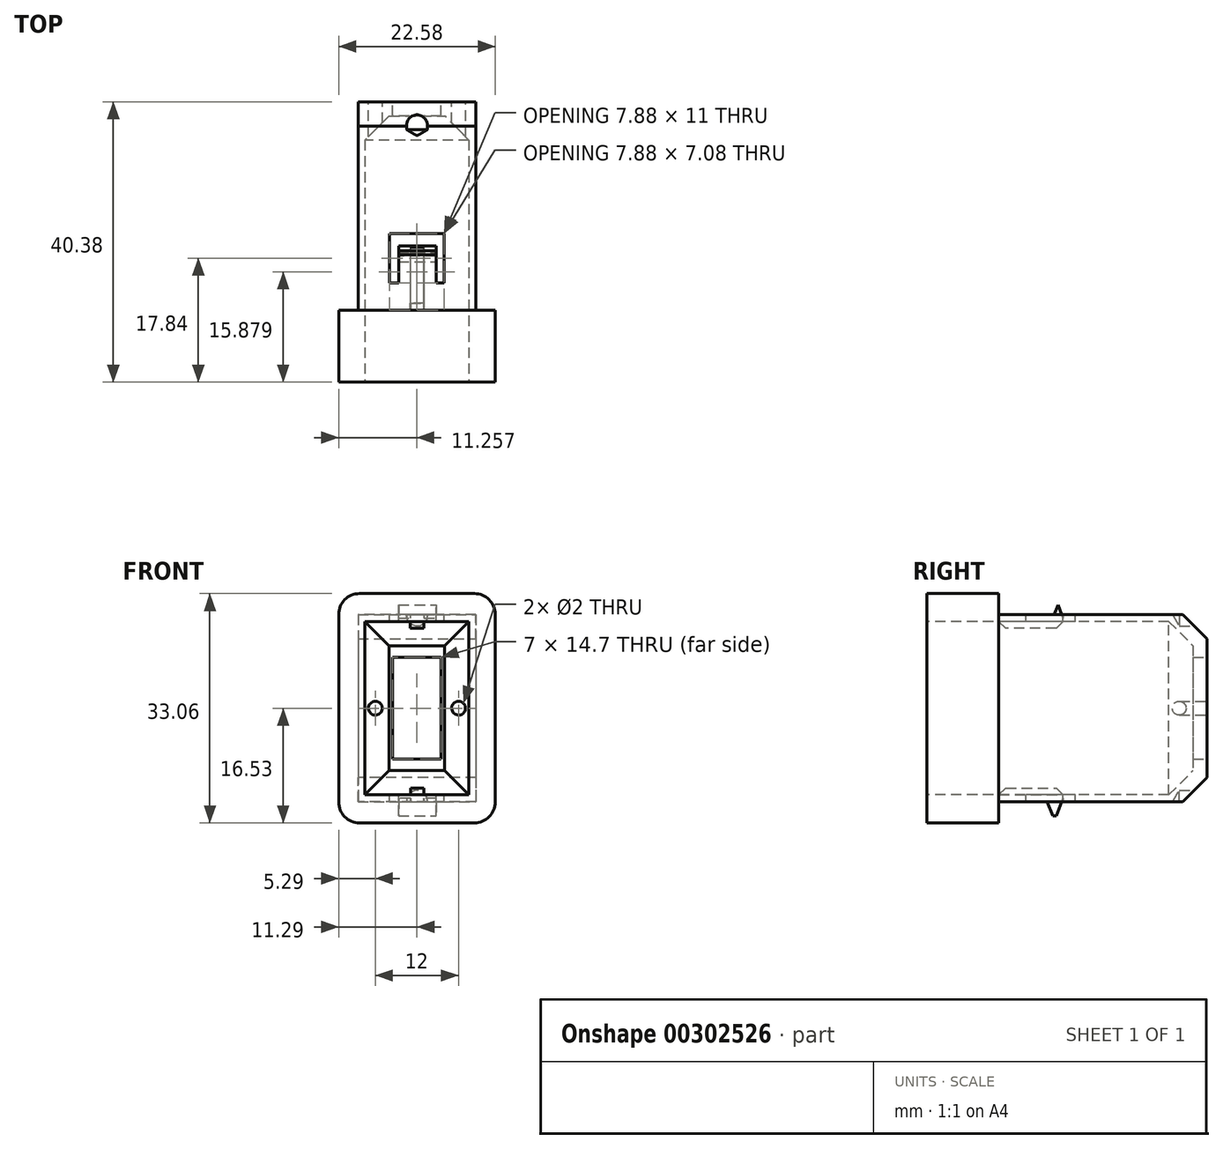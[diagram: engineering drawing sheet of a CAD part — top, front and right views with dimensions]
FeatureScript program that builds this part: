
annotation { "Feature Type Name" : "Feature", "Feature Type Description" : "" }
export const myFeature = defineFeature(function(context is Context, id is Id, definition is map)
    precondition{}
    {
        {
            assignVariable(context, id + "F0", {"name" : "face_depth", "anyValue" : 10.38});
        }
        {
            assignVariable(context, id + "F1", {"name" : "neck_height", "anyValue" : 27});
        }
        {
            assignVariable(context, id + "F2", {"name" : "neck_tab_hieght", "anyValue" : 31});
        }
        {
            assignVariable(context, id + "F3", {"name" : "neck_depth", "anyValue" : 30});
        }
        {
            var Q0;
            Q0=qCreatedBy(makeId("Front.planeOp"),FACE);
            var sketch = newSketch(context, id + "F4", { "sketchPlane" : qUnion([Q0])});
            skLineSegment(sketch, "E0.bottom", {"start": v(8.5, 13.5) * mm, "end": v(-8.5, 13.5) * mm});
            skLineSegment(sketch, "E0.top", {"start": v(8.5, -13.5) * mm, "end": v(-8.5, -13.5) * mm});
            skLineSegment(sketch, "E0.left", {"start": v(8.5, 13.5) * mm, "end": v(8.5, -13.5) * mm});
            skLineSegment(sketch, "E0.right", {"start": v(-8.5, 13.5) * mm, "end": v(-8.5, -13.5) * mm});
            skPoint(sketch, "E0.middle", {"position": v(0, 0) * mm});
            skLineSegment(sketch, "E1.bottom", {"start": v(11.29, -16.52) * mm, "end": v(-11.29, -16.53) * mm});
            skLineSegment(sketch, "E1.top", {"start": v(11.3, 16.52) * mm, "end": v(-11.29, 16.52) * mm});
            skLineSegment(sketch, "E1.left", {"start": v(11.29, -16.52) * mm, "end": v(11.3, 16.52) * mm});
            skLineSegment(sketch, "E1.right", {"start": v(-11.29, -16.52) * mm, "end": v(-11.29, 16.52) * mm});
            skSolve(sketch);
        }
        {
            var Q0;
            Q0=makeQuery(id+"F4.imprint","IMPRINT",FACE,{"disambiguationData":[TD([[makeQuery(id+"F4.imprint","IMPRINT",EDGE,{"derivedFrom":sQuery(id+"F4.wireOp",EDGE,"E0.bottom")}),1.0]])]});
            extrude(context, id + "F5", {"entities" : qUnion([Q0]), "oppositeDirection" : true, "depth" : (getVariable(context, 'neck_depth')) * mm});
        }
        {
            var Q0;
            Q0=makeQuery(id+"F4.imprint","IMPRINT",FACE,{"disambiguationData":[TD([[makeQuery(id+"F4.imprint","IMPRINT",EDGE,{"derivedFrom":sQuery(id+"F4.wireOp",EDGE,"E0.bottom")}),-1.0]])]});
            var Q1;
            Q1=makeQuery(id+"F4.imprint","IMPRINT",FACE,{"disambiguationData":[TD([[makeQuery(id+"F4.imprint","IMPRINT",EDGE,{"derivedFrom":sQuery(id+"F4.wireOp",EDGE,"E0.bottom")}),1.0]])]});
            extrude(context, id + "F6", {"entities" : qUnion([Q0, Q1]), "operationType" : NewBodyOperationType.ADD, "depth" : (getVariable(context, 'face_depth')) * mm});
        }
        {
            var Q0;
            Q0=makeQuery(id+"F6.opExtrude","CAP_FACE",FACE,{"disambiguationData":[OSD([sQuery(id+"F4.wireOp",EDGE,"E1.bottom"),sQuery(id+"F4.wireOp",EDGE,"E1.top"),sQuery(id+"F4.wireOp",EDGE,"E1.left"),sQuery(id+"F4.wireOp",EDGE,"E1.right")])],"isStart":false});
            var sketch = newSketch(context, id + "F7", { "sketchPlane" : qUnion([Q0])});
            skLineSegment(sketch, "E2.bottom", {"start": v(-7.5, 12.5) * mm, "end": v(7.5, 12.5) * mm});
            skLineSegment(sketch, "E2.top", {"start": v(-7.5, -12.5) * mm, "end": v(7.5, -12.5) * mm});
            skLineSegment(sketch, "E2.left", {"start": v(-7.5, 12.5) * mm, "end": v(-7.5, -12.5) * mm});
            skLineSegment(sketch, "E2.right", {"start": v(7.5, 12.5) * mm, "end": v(7.5, -12.5) * mm});
            skPoint(sketch, "E2.middle", {"position": v(0, 0) * mm});
            skSolve(sketch);
        }
        {
            var Q0;
            Q0=makeQuery(id+"F7.imprint","IMPRINT",FACE,{"disambiguationData":[TD([[makeQuery(id+"F7.imprint","IMPRINT",EDGE,{"derivedFrom":sQuery(id+"F7.wireOp",EDGE,"E2.bottom")}),-1.0]])]});
            extrude(context, id + "F8", {"entities" : qUnion([Q0]), "operationType" : NewBodyOperationType.REMOVE, "oppositeDirection" : true, "depth" : (getVariable(context, 'face_depth') + getVariable(context, 'neck_depth') - 2) * mm});
        }
        {
            var Q0;
            Q0=makeQuery(id+"F5.opExtrude","CAP_FACE",FACE,{"disambiguationData":[OSD([sQuery(id+"F4.wireOp",EDGE,"E0.bottom"),sQuery(id+"F4.wireOp",EDGE,"E0.top"),sQuery(id+"F4.wireOp",EDGE,"E0.left"),sQuery(id+"F4.wireOp",EDGE,"E0.right")])],"isStart":false});
            var sketch = newSketch(context, id + "F9", { "sketchPlane" : qUnion([Q0])});
            skLineSegment(sketch, "E3.bottom", {"start": v(3.5, -7.35) * mm, "end": v(-3.5, -7.35) * mm});
            skLineSegment(sketch, "E3.top", {"start": v(3.5, 7.35) * mm, "end": v(-3.5, 7.35) * mm});
            skLineSegment(sketch, "E3.left", {"start": v(3.5, -7.35) * mm, "end": v(3.5, 7.35) * mm});
            skLineSegment(sketch, "E3.right", {"start": v(-3.5, -7.35) * mm, "end": v(-3.5, 7.35) * mm});
            skPoint(sketch, "E3.middle", {"position": v(0, 0) * mm});
            skSolve(sketch);
        }
        {
            var Q0;
            Q0=makeQuery(id+"F9.imprint","IMPRINT",FACE,{"disambiguationData":[TD([[makeQuery(id+"F9.imprint","IMPRINT",EDGE,{"derivedFrom":sQuery(id+"F9.wireOp",EDGE,"E3.bottom")}),-1.0]])]});
            extrude(context, id + "F10", {"entities" : qUnion([Q0]), "operationType" : NewBodyOperationType.REMOVE, "oppositeDirection" : true, "depth" : 25 * mm});
        }
        {
            var Q0;
            Q0=makeQuery(id+"F5.opExtrude","SWEPT_FACE",FACE,{"disambiguationData":[OSD([sQuery(id+"F4.wireOp",EDGE,"E0.bottom")])]});
            var sketch = newSketch(context, id + "F11", { "sketchPlane" : qUnion([Q0])});
            skLineSegment(sketch, "E4.bottom", {"start": v(-3.97, 3.92) * mm, "end": v(3.9, 3.92) * mm});
            skLineSegment(sketch, "E4.top", {"start": v(-3.97, 11) * mm, "end": v(3.9, 11) * mm});
            skLineSegment(sketch, "E4.left", {"start": v(-3.97, 3.92) * mm, "end": v(-3.97, 11) * mm});
            skLineSegment(sketch, "E4.right", {"start": v(3.9, 3.92) * mm, "end": v(3.9, 11) * mm});
            skLineSegment(sketch, "E5.bottom", {"start": v(-2.64, 3.92) * mm, "end": v(2.75, 3.92) * mm});
            skLineSegment(sketch, "E5.top", {"start": v(-2.64, 9.27) * mm, "end": v(2.75, 9.27) * mm});
            skLineSegment(sketch, "E5.left", {"start": v(-2.64, 3.92) * mm, "end": v(-2.64, 9.27) * mm});
            skLineSegment(sketch, "E5.right", {"start": v(2.75, 3.92) * mm, "end": v(2.75, 9.27) * mm});
            skLineSegment(sketch, "E6", {"start": v(-2.64, 7.77) * mm, "end": v(2.75, 7.77) * mm});
            skSolve(sketch);
        }
        {
            var Q0;
            Q0=makeQuery(id+"F11.imprint","IMPRINT",FACE,{"disambiguationData":[TD([[makeQuery(id+"F11.imprint","IMPRINT",EDGE,{"derivedFrom":sQuery(id+"F11.wireOp",EDGE,"E4.top")}),-1.0]])]});
            extrude(context, id + "F12", {"entities" : qUnion([Q0]), "operationType" : NewBodyOperationType.REMOVE, "oppositeDirection" : true, "depth" : 100 * mm});
        }
        {
            var Q0;
            {var subQ0=sQuery(id+"F11.wireOp",EDGE,"E5.top");Q0=makeQuery(id+"F11.imprint","IMPRINT",FACE,{"disambiguationData":[TD([[makeQuery(id+"F11.imprint","IMPRINT",EDGE,{"derivedFrom":subQ0}),-1.0]])]});}
            extrude(context, id + "F13", {"entities" : qUnion([Q0]), "operationType" : NewBodyOperationType.ADD, "depth" : (getVariable(context, 'neck_tab_hieght') - getVariable(context, 'neck_height')) / 2 * mm});
        }
        {
            var Q0;
            Q0=makeQuery(id+"F13.opExtrude","CAP_EDGE",EDGE,{"disambiguationData":[OSD([sQuery(id+"F11.wireOp",EDGE,"E6")])],"isStart":false});
            var Q1;
            Q1=makeQuery(id+"F13.opExtrude","CAP_EDGE",EDGE,{"disambiguationData":[OSD([sQuery(id+"F11.wireOp",EDGE,"E5.top")])],"isStart":false});
            chamfer(context, id + "F14", {"entities" : qUnion([Q0, Q1]), "chamferType" : ChamferType.TWO_OFFSETS, "width1" : 1 * mm, "oppositeDirection" : false, "width2" : 2.5 * mm, "tangentPropagation" : true});
        }
        {
            var Q0;
            Q0=makeQuery(id+"F5.opExtrude","SWEPT_FACE",FACE,{"disambiguationData":[OSD([sQuery(id+"F4.wireOp",EDGE,"E0.top")])]});
            var sketch = newSketch(context, id + "F15", { "sketchPlane" : qUnion([Q0])});
            skLineSegment(sketch, "E7", {"start": v(2.75, -6.77) * mm, "end": v(-2.64, -6.77) * mm});
            skSolve(sketch);
        }
        {
            var Q0;
            {var subQ0=sQuery(id+"F15.wireOp",EDGE,"E7");Q0=makeQuery(id+"F15.imprint","IMPRINT",FACE,{"disambiguationData":[TD([[makeQuery(id+"F15.imprint","IMPRINT",EDGE,{"derivedFrom":subQ0}),1.0]])]});}
            extrude(context, id + "F16", {"entities" : qUnion([Q0]), "operationType" : NewBodyOperationType.ADD, "depth" : (getVariable(context, 'neck_tab_hieght') - getVariable(context, 'neck_height')) / 2 * mm});
        }
        {
            var Q0;
            Q0=makeQuery(id+"F16.opExtrude","CAP_EDGE",EDGE,{"disambiguationData":[OSD([sQuery(id+"F15.wireOp",EDGE,"E7")])],"isStart":false});
            var Q1;
            Q1=makeQuery(id+"F16.opExtrude","CAP_EDGE",EDGE,{"disambiguationData":[OSD([sQuery(id+"F4.wireOp",EDGE,"E0.top"),sQuery(id+"F11.wireOp",EDGE,"E5.top")])],"isStart":false});
            chamfer(context, id + "F17", {"entities" : qUnion([Q0, Q1]), "chamferType" : ChamferType.TWO_OFFSETS, "width1" : 1 * mm, "oppositeDirection" : false, "width2" : 2.5 * mm, "tangentPropagation" : true});
        }
        {
            var Q0;
            Q0=makeQuery(id+"F8.boolean.opBoolean","COPY",EDGE,{"derivedFrom":makeQuery(id+"F8.opExtrude","CAP_EDGE",EDGE,{"disambiguationData":[OSD([sQuery(id+"F7.wireOp",EDGE,"E2.right")])],"isStart":false})});
            var Q1;
            Q1=makeQuery(id+"F8.boolean.opBoolean","COPY",EDGE,{"derivedFrom":makeQuery(id+"F8.opExtrude","CAP_EDGE",EDGE,{"disambiguationData":[OSD([sQuery(id+"F7.wireOp",EDGE,"E2.left")])],"isStart":false})});
            var Q2;
            Q2=makeQuery(id+"F8.boolean.opBoolean","COPY",EDGE,{"derivedFrom":makeQuery(id+"F8.opExtrude","CAP_EDGE",EDGE,{"disambiguationData":[OSD([sQuery(id+"F7.wireOp",EDGE,"E2.bottom")])],"isStart":false})});
            var Q3;
            Q3=makeQuery(id+"F8.boolean.opBoolean","COPY",EDGE,{"derivedFrom":makeQuery(id+"F8.opExtrude","CAP_EDGE",EDGE,{"disambiguationData":[OSD([sQuery(id+"F7.wireOp",EDGE,"E2.top")])],"isStart":false})});
            var Q4;
            Q4=makeQuery(id+"F5.opExtrude","CAP_EDGE",EDGE,{"disambiguationData":[OSD([sQuery(id+"F4.wireOp",EDGE,"E0.bottom")])],"isStart":false});
            var Q5;
            Q5=makeQuery(id+"F5.opExtrude","CAP_EDGE",EDGE,{"disambiguationData":[OSD([sQuery(id+"F4.wireOp",EDGE,"E0.top")])],"isStart":false});
            chamfer(context, id + "F18", {"entities" : qUnion([Q0, Q1, Q2, Q3, Q4, Q5]), "width" : 3.5 * mm, "tangentPropagation" : true});
        }
        {
            var Q0;
            Q0=makeQuery(id+"F6.opExtrude","SWEPT_EDGE",EDGE,{"disambiguationData":[OSD([sQuery(id+"F4.wireOp",EDGE,"E1.top"),sQuery(id+"F4.wireOp",EDGE,"E1.right")])]});
            var Q1;
            Q1=makeQuery(id+"F6.opExtrude","SWEPT_EDGE",EDGE,{"disambiguationData":[OSD([sQuery(id+"F4.wireOp",EDGE,"E1.top"),sQuery(id+"F4.wireOp",EDGE,"E1.left")])]});
            var Q2;
            Q2=makeQuery(id+"F6.opExtrude","SWEPT_EDGE",EDGE,{"disambiguationData":[OSD([sQuery(id+"F4.wireOp",EDGE,"E1.bottom"),sQuery(id+"F4.wireOp",EDGE,"E1.left")])]});
            var Q3;
            Q3=makeQuery(id+"F6.opExtrude","SWEPT_EDGE",EDGE,{"disambiguationData":[OSD([sQuery(id+"F4.wireOp",EDGE,"E1.bottom"),sQuery(id+"F4.wireOp",EDGE,"E1.right")])]});
            fillet(context, id + "F19", {"entities" : qUnion([Q0, Q1, Q2, Q3]), "radius" : 3 * mm, "tangentPropagation" : true, "allowEdgeOverflow" : false});
        }
        {
            var Q0;
            Q0=makeQuery(id+"F5.opExtrude","CAP_FACE",FACE,{"disambiguationData":[OSD([sQuery(id+"F4.wireOp",EDGE,"E0.bottom"),sQuery(id+"F4.wireOp",EDGE,"E0.top"),sQuery(id+"F4.wireOp",EDGE,"E0.left"),sQuery(id+"F4.wireOp",EDGE,"E0.right")])],"isStart":false});
            var sketch = newSketch(context, id + "F20", { "sketchPlane" : qUnion([Q0])});
            skPoint(sketch, "E8", {"position": v(-6, 0) * mm});
            skPoint(sketch, "E8.positionSnap0", {"position": v(-3.5, 0) * mm});
            skPoint(sketch, "E9", {"position": v(6, 0) * mm});
            skPoint(sketch, "E9.positionSnap0", {"position": v(3.5, 0) * mm});
            skPoint(sketch, "E10", {"position": v(0, 13.35) * mm});
            skPoint(sketch, "E10.positionSnap0", {"position": v(0, 7.35) * mm});
            skPoint(sketch, "E11", {"position": v(0, -13.35) * mm});
            skPoint(sketch, "E11.positionSnap0", {"position": v(0, -7.35) * mm});
            skSolve(sketch);
        }
        {
            var Q0;
            Q0=sQuery(id+"F20.wireOp",VERTEX,"E8");
            var Q1;
            Q1=sQuery(id+"F20.wireOp",VERTEX,"E9");
            var Q2;
            Q2=makeQuery(id+"F5.opExtrude","SWEPT_BODY",BODY,{"disambiguationData":[OSD([sQuery(id+"F4.wireOp",EDGE,"E0.bottom"),sQuery(id+"F4.wireOp",EDGE,"E0.top"),sQuery(id+"F4.wireOp",EDGE,"E0.left"),sQuery(id+"F4.wireOp",EDGE,"E0.right")])]});
            hole(context, id + "F21", {"style" : HoleStyle.SIMPLE, "endStyle" : HoleEndStyle.BLIND, "holeDiameter" : 2 * mm, "holeDepth" : 6 * mm, "isTappedThrough" : true, "tappedDepth" : 12 * mm, "tapClearance" : 3, "locations" : qUnion([Q0, Q1]), "scope" : qUnion([Q2])});
        }
        {
            var Q0;
            Q0=sQuery(id+"F20.wireOp",VERTEX,"E10");
            var Q1;
            Q1=sQuery(id+"F20.wireOp",VERTEX,"E11");
            var Q2;
            Q2=makeQuery(id+"F5.opExtrude","SWEPT_BODY",BODY,{"disambiguationData":[OSD([sQuery(id+"F4.wireOp",EDGE,"E0.bottom"),sQuery(id+"F4.wireOp",EDGE,"E0.top"),sQuery(id+"F4.wireOp",EDGE,"E0.left"),sQuery(id+"F4.wireOp",EDGE,"E0.right")])]});
            hole(context, id + "F22", {"style" : HoleStyle.SIMPLE, "endStyle" : HoleEndStyle.BLIND, "holeDiameter" : 3 * mm, "holeDepth" : 4 * mm, "isTappedThrough" : true, "tappedDepth" : 12 * mm, "tapClearance" : 3, "locations" : qUnion([Q0, Q1]), "scope" : qUnion([Q2])});
        }
        {
            var Q0;
            Q0=makeQuery(id+"F8.boolean.opBoolean","COPY",FACE,{"derivedFrom":makeQuery(id+"F8.opExtrude","SWEPT_FACE",FACE,{"disambiguationData":[OSD([sQuery(id+"F7.wireOp",EDGE,"E2.bottom")])]})});
            var sketch = newSketch(context, id + "F23", { "sketchPlane" : qUnion([Q0])});
            skLineSegment(sketch, "E12.bottom", {"start": v(1, -9.27) * mm, "end": v(-0.95, -9.27) * mm});
            skLineSegment(sketch, "E12.top", {"start": v(1, 0) * mm, "end": v(-0.95, 0) * mm});
            skLineSegment(sketch, "E12.left", {"start": v(1, -9.27) * mm, "end": v(1, 0) * mm});
            skLineSegment(sketch, "E12.right", {"start": v(-0.95, -9.27) * mm, "end": v(-0.95, 0) * mm});
            skPoint(sketch, "E12.middle", {"position": v(0.03, -4.63) * mm});
            skSolve(sketch);
        }
        {
            var Q0;
            Q0=makeQuery(id+"F8.boolean.opBoolean","COPY",FACE,{"derivedFrom":makeQuery(id+"F8.opExtrude","SWEPT_FACE",FACE,{"disambiguationData":[OSD([sQuery(id+"F7.wireOp",EDGE,"E2.top")])]})});
            var sketch = newSketch(context, id + "F24", { "sketchPlane" : qUnion([Q0])});
            skLineSegment(sketch, "E13.bottom", {"start": v(1, 0) * mm, "end": v(-0.94, 0) * mm});
            skLineSegment(sketch, "E13.top", {"start": v(1, 9.27) * mm, "end": v(-0.94, 9.27) * mm});
            skLineSegment(sketch, "E13.left", {"start": v(1, 0) * mm, "end": v(1, 9.27) * mm});
            skLineSegment(sketch, "E13.right", {"start": v(-0.94, 0) * mm, "end": v(-0.94, 9.27) * mm});
            skPoint(sketch, "E13.middle", {"position": v(0.03, 4.63) * mm});
            skSolve(sketch);
        }
        {
            var Q0;
            Q0 = qSketchRegion(id + "F24", true);
            var Q1;
            Q1 = qSketchRegion(id + "F23", true);
            extrude(context, id + "F25", {"entities" : qUnion([Q0, Q1]), "operationType" : NewBodyOperationType.ADD, "endBound" : BoundingType.SYMMETRIC, "depth" : 2 * mm});
        }
        {
            var Q0;
            Q0=makeQuery(id+"F25.opExtrude","CAP_EDGE",EDGE,{"disambiguationData":[OSD([sQuery(id+"F23.wireOp",EDGE,"E12.top")])],"isStart":true});
            var Q1;
            Q1=makeQuery(id+"F25.opExtrude","CAP_EDGE",EDGE,{"disambiguationData":[OSD([sQuery(id+"F23.wireOp",EDGE,"E12.bottom")])],"isStart":true});
            var Q2;
            Q2=makeQuery(id+"F25.opExtrude","CAP_EDGE",EDGE,{"disambiguationData":[OSD([sQuery(id+"F24.wireOp",EDGE,"E13.top")])],"isStart":false});
            var Q3;
            Q3=makeQuery(id+"F25.opExtrude","CAP_EDGE",EDGE,{"disambiguationData":[OSD([sQuery(id+"F24.wireOp",EDGE,"E13.bottom")])],"isStart":false});
            chamfer(context, id + "F26", {"entities" : qUnion([Q0, Q1, Q2, Q3]), "width" : 1 * mm, "tangentPropagation" : true});
        }
    });
